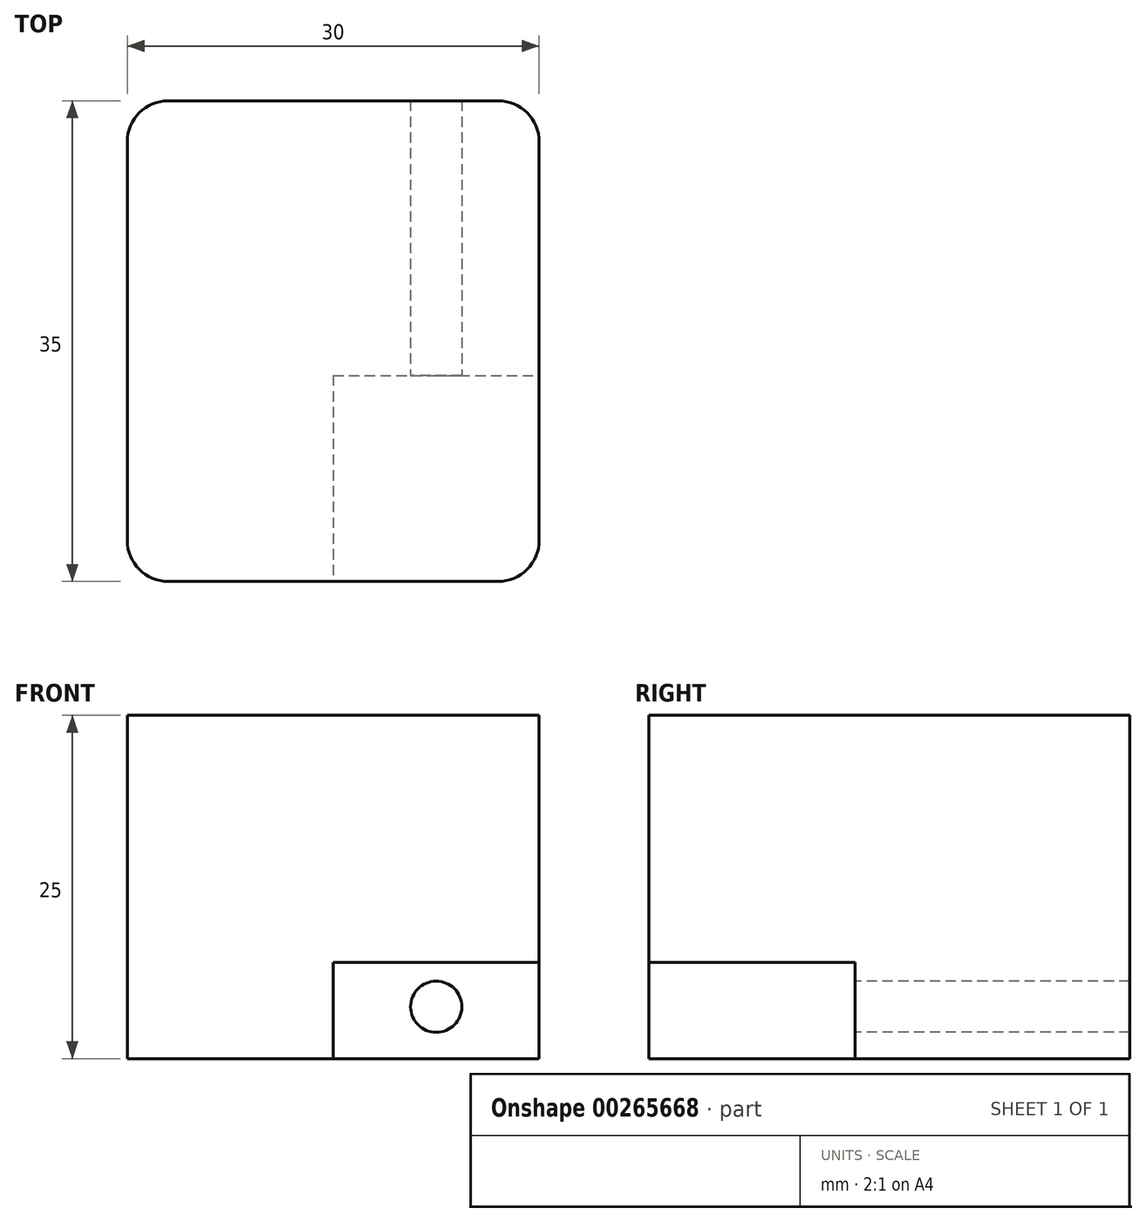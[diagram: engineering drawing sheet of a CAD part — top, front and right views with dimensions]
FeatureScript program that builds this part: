
annotation { "Feature Type Name" : "Feature", "Feature Type Description" : "" }
export const myFeature = defineFeature(function(context is Context, id is Id, definition is map)
    precondition{}
    {
        {
            var Q0;
            Q0=qCreatedBy(makeId("Front.planeOp"),FACE);
            var sketch = newSketch(context, id + "F0", { "sketchPlane" : qUnion([Q0])});
            skLineSegment(sketch, "E0.bottom", {"start": v(0, 0) * mm, "end": v(30, 0) * mm});
            skLineSegment(sketch, "E0.top", {"start": v(0, -25) * mm, "end": v(30, -25) * mm});
            skLineSegment(sketch, "E0.left", {"start": v(0, 0) * mm, "end": v(0, -25) * mm});
            skLineSegment(sketch, "E0.right", {"start": v(30, 0) * mm, "end": v(30, -25) * mm});
            skSolve(sketch);
        }
        {
            var Q0;
            Q0=makeQuery(id+"F0.imprint","IMPRINT",FACE,{"disambiguationData":[TD([[makeQuery(id+"F0.imprint","IMPRINT",EDGE,{"derivedFrom":sQuery(id+"F0.wireOp",EDGE,"E0.bottom")}),-1.0]])]});
            extrude(context, id + "F1", {"entities" : qUnion([Q0]), "depth" : 35 * mm});
        }
        {
            var Q0;
            Q0=makeQuery(id+"F1.opExtrude","CAP_FACE",FACE,{"disambiguationData":[OSD([sQuery(id+"F0.wireOp",EDGE,"E0.bottom"),sQuery(id+"F0.wireOp",EDGE,"E0.top"),sQuery(id+"F0.wireOp",EDGE,"E0.left"),sQuery(id+"F0.wireOp",EDGE,"E0.right")])],"isStart":false});
            var sketch = newSketch(context, id + "F2", { "sketchPlane" : qUnion([Q0])});
            skLineSegment(sketch, "E1.bottom", {"start": v(30, -25) * mm, "end": v(15, -25) * mm});
            skLineSegment(sketch, "E1.top", {"start": v(30, -18) * mm, "end": v(15, -18) * mm});
            skLineSegment(sketch, "E1.left", {"start": v(30, -25) * mm, "end": v(30, -18) * mm});
            skLineSegment(sketch, "E1.right", {"start": v(15, -25) * mm, "end": v(15, -18) * mm});
            skSolve(sketch);
        }
        {
            var Q0;
            Q0 = qSketchRegion(id + "F2", true);
            extrude(context, id + "F3", {"entities" : qUnion([Q0]), "operationType" : NewBodyOperationType.REMOVE, "oppositeDirection" : true, "depth" : 15 * mm});
        }
        {
            var Q0;
            Q0=makeQuery(id+"F3.boolean.opBoolean","COPY",FACE,{"derivedFrom":makeQuery(id+"F3.opExtrude","CAP_FACE",FACE,{"disambiguationData":[OSD([sQuery(id+"F2.wireOp",EDGE,"E1.bottom"),sQuery(id+"F2.wireOp",EDGE,"E1.top"),sQuery(id+"F2.wireOp",EDGE,"E1.left"),sQuery(id+"F2.wireOp",EDGE,"E1.right")])],"isStart":false})});
            var sketch = newSketch(context, id + "F4", { "sketchPlane" : qUnion([Q0])});
            skCircle(sketch, "E2", {"center": v(22.5, -21.22) * mm, "radius": 1.87 * mm});
            skPoint(sketch, "E2.centerSnap0", {"position": v(22.5, -18) * mm});
            skSolve(sketch);
        }
        {
            var Q0;
            Q0=makeQuery(id+"F4.imprint","IMPRINT",FACE,{"disambiguationData":[TD([[makeQuery(id+"F4.imprint","IMPRINT",EDGE,{"derivedFrom":sQuery(id+"F4.wireOp",EDGE,"E2")}),1.0]])]});
            extrude(context, id + "F5", {"entities" : qUnion([Q0]), "operationType" : NewBodyOperationType.REMOVE, "endBound" : BoundingType.THROUGH_ALL, "oppositeDirection" : true, "depth" : 3 * mm});
        }
        {
            var Q0;
            Q0=makeQuery(id+"F1.opExtrude","CAP_EDGE",EDGE,{"disambiguationData":[OSD([sQuery(id+"F0.wireOp",EDGE,"E0.left")])],"isStart":false});
            var Q1;
            Q1=makeQuery(id+"F3.boolean.opBoolean","COPY",EDGE,{"derivedFrom":makeQuery(id+"F3.opExtrude","CAP_EDGE",EDGE,{"disambiguationData":[OSD([sQuery(id+"F2.wireOp",EDGE,"E1.right")])],"isStart":true})});
            var Q2;
            Q2=makeQuery(id+"F1.opExtrude","CAP_EDGE",EDGE,{"disambiguationData":[OSD([sQuery(id+"F0.wireOp",EDGE,"E0.right")])],"isStart":true});
            var Q3;
            Q3=makeQuery(id+"F1.opExtrude","CAP_EDGE",EDGE,{"disambiguationData":[OSD([sQuery(id+"F0.wireOp",EDGE,"E0.right")])],"isStart":false});
            var Q4;
            Q4=makeQuery(id+"F3.boolean.opBoolean","COPY",EDGE,{"derivedFrom":makeQuery(id+"F3.opExtrude","CAP_EDGE",EDGE,{"disambiguationData":[OSD([sQuery(id+"F2.wireOp",EDGE,"E1.left")])],"isStart":false})});
            var Q5;
            Q5=makeQuery(id+"F1.opExtrude","CAP_EDGE",EDGE,{"disambiguationData":[OSD([sQuery(id+"F0.wireOp",EDGE,"E0.left")])],"isStart":true});
            fillet(context, id + "F6", {"entities" : qUnion([Q0, Q1, Q2, Q3, Q4, Q5]), "radius" : 3 * mm, "tangentPropagation" : true, "allowEdgeOverflow" : false});
        }
    });
